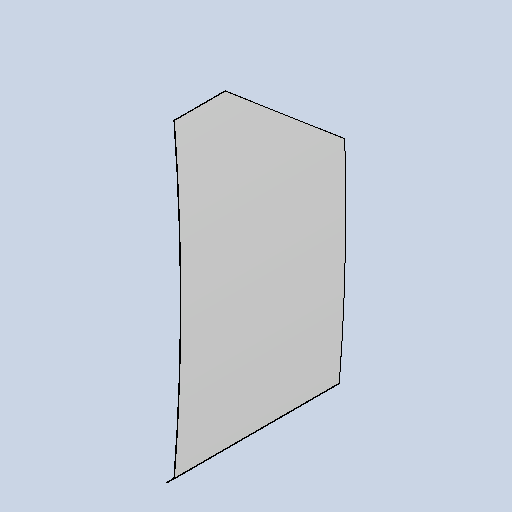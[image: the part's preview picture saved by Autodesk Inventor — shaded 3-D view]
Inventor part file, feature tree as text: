
AUTODESK INVENTOR PART (.ipt)
format: ipt  version: 2025 (Build 290162010, 162A)  size: 507,392 bytes
history: native  units: mm
features: other x4, sheet_metal_op x3, sketch x3, extrude x1, projected_geometry x1
ambient origin geometry x8: Origin, YZ Plane, XZ Plane, XY Plane, X Axis, Y Axis, Z Axis, Center Point
bodies: Body1 (feature_tree)
feature tree (12):
  sheet_metal_op  "Contour Flange2"
  extrude  "Extrusion2"  Depth=3.0mm
  other  "Mark5"
  other  "A-Side Definition"
  sketch  "Sketch1"  dims[d36=3.0mm d37=3.0mm]
  other  "Plate2"
  sheet_metal_op  "Bend2"
  sheet_metal_op  "Corner2"
  sketch  "Sketch2"  dims[d38=1.5mm]
  projected_geometry  "Projected Loop3"
  sketch  "Sketch6"  dims[d39=6.0mm d40=5.0mm d41=980.0mm d42=5.0mm d43=3.0mm d44=12.0mm d45=3.0mm d46=5.0mm d65=8.0mm d66=8.0mm d69=3.0mm d78=3.0mm d80=3.0mm d123=0.0mm d124=0.0mm d155=5.0mm d156=63.0mm d157=11050.0mm d158=23.736478mm d160=5.0mm d161=6.981317mm d162=304.0mm d164=304.0mm d165=6.981317mm d166=12.0mm d167=12.0mm d168=0.0mm d169=1843.0mm]
  other  "Definition1"
